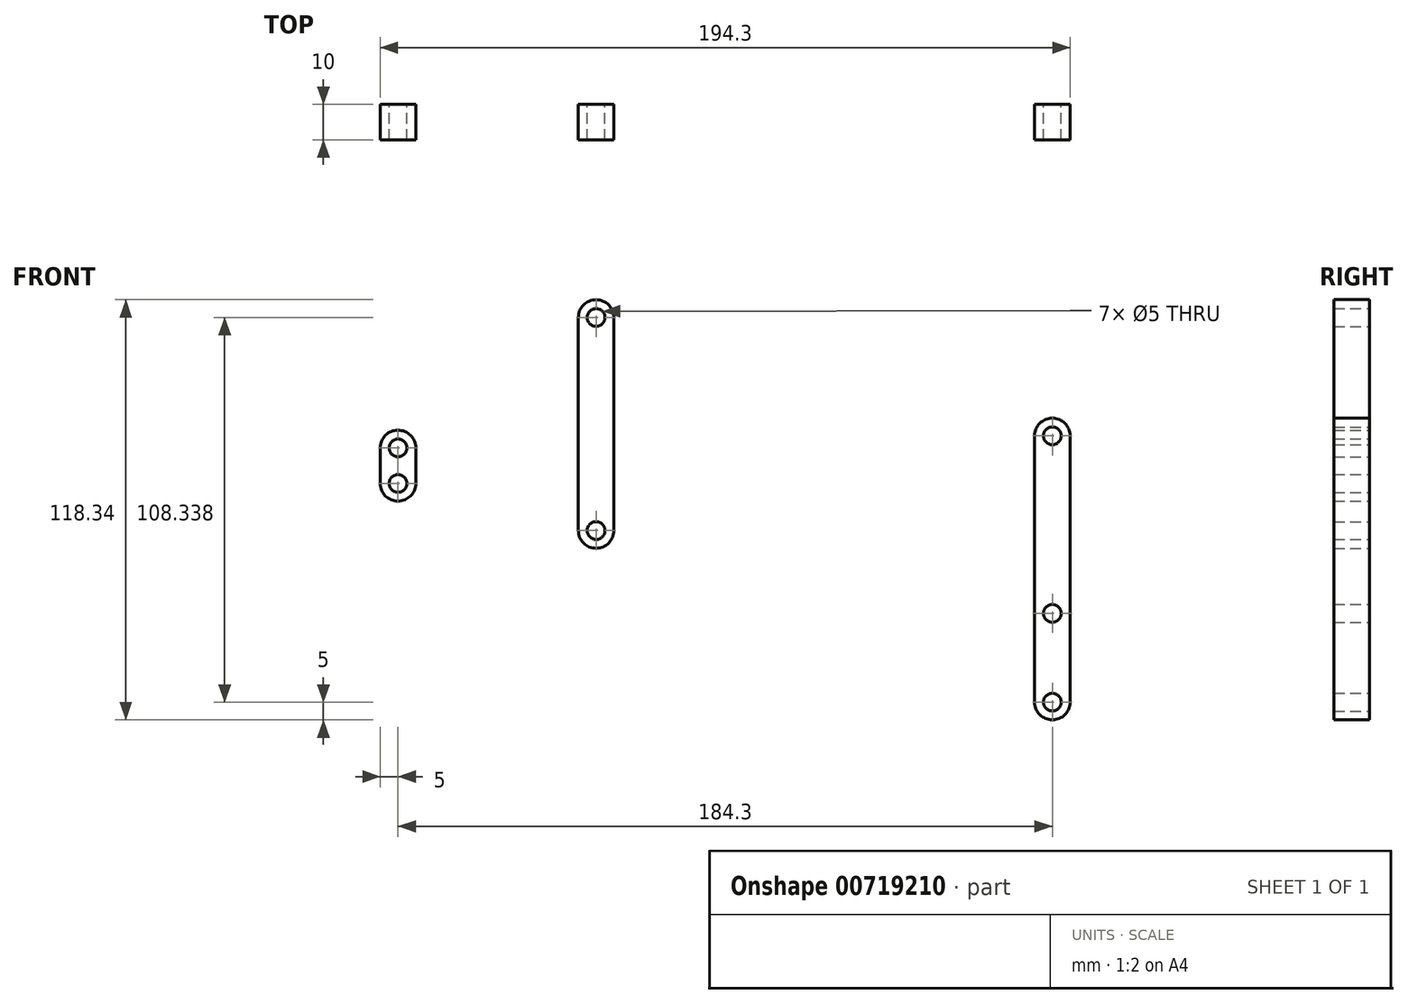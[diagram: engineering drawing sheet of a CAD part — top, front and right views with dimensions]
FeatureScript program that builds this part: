
annotation { "Feature Type Name" : "Feature", "Feature Type Description" : "" }
export const myFeature = defineFeature(function(context is Context, id is Id, definition is map)
    precondition{}
    {
        {
            var Q0;
            Q0=qCreatedBy(makeId("Front.planeOp"),FACE);
            var sketch = newSketch(context, id + "F0", { "sketchPlane" : qUnion([Q0])});
            skLineSegment(sketch, "E0.left", {"start": v(-5, 37.5) * mm, "end": v(-5, -37.5) * mm});
            skLineSegment(sketch, "E0.right", {"start": v(5, 37.5) * mm, "end": v(5, -37.5) * mm});
            skPoint(sketch, "E0.middle", {"position": v(0, 0) * mm});
            skArc(sketch, "E1", {"start": v(5, 37.5) * mm, "mid": v(0, 42.5) * mm, "end": v(-5, 37.5) * mm});
            skArc(sketch, "E2", {"start": v(-5, -37.5) * mm, "mid": v(0, -42.5) * mm, "end": v(5, -37.5) * mm});
            skCircle(sketch, "E3", {"center": v(0, 37.5) * mm, "radius": 2.5 * mm});
            skCircle(sketch, "E4", {"center": v(0, -37.5) * mm, "radius": 2.5 * mm});
            skCircle(sketch, "E5", {"center": v(0, -12.5) * mm, "radius": 2.5 * mm});
            skSolve(sketch);
        }
        {
            var Q0;
            Q0=makeQuery(id+"F0.imprint","IMPRINT",FACE,{"disambiguationData":[TD([[makeQuery(id+"F0.imprint","IMPRINT",EDGE,{"derivedFrom":sQuery(id+"F0.wireOp",EDGE,"E0.left")}),1.0]])]});
            extrude(context, id + "F1", {"entities" : qUnion([Q0]), "depth" : 10 * mm, "offsetDistance" : 25 * mm});
        }
        {
            var Q0;
            Q0=qCreatedBy(makeId("Front.planeOp"),FACE);
            var sketch = newSketch(context, id + "F2", { "sketchPlane" : qUnion([Q0])});
            skLineSegment(sketch, "E6.left", {"start": v(-133.5, 70.84) * mm, "end": v(-133.5, 10.84) * mm});
            skLineSegment(sketch, "E6.right", {"start": v(-123.5, 70.84) * mm, "end": v(-123.5, 10.84) * mm});
            skPoint(sketch, "E6.middle", {"position": v(-128.5, 40.84) * mm});
            skArc(sketch, "E7", {"start": v(-123.5, 70.84) * mm, "mid": v(-128.5, 75.84) * mm, "end": v(-133.5, 70.84) * mm});
            skArc(sketch, "E8", {"start": v(-133.5, 10.84) * mm, "mid": v(-128.5, 5.84) * mm, "end": v(-123.5, 10.84) * mm});
            skCircle(sketch, "E9", {"center": v(-128.5, 70.84) * mm, "radius": 2.5 * mm});
            skCircle(sketch, "E10", {"center": v(-128.5, 10.84) * mm, "radius": 2.5 * mm});
            skSolve(sketch);
        }
        {
            var Q0;
            Q0=makeQuery(id+"F2.imprint","IMPRINT",FACE,{"disambiguationData":[TD([[makeQuery(id+"F2.imprint","IMPRINT",EDGE,{"derivedFrom":sQuery(id+"F2.wireOp",EDGE,"E6.left")}),1.0]])]});
            extrude(context, id + "F3", {"entities" : qUnion([Q0]), "depth" : 10 * mm, "offsetDistance" : 25 * mm});
        }
        {
            var Q0;
            Q0=qCreatedBy(makeId("Front.planeOp"),FACE);
            var sketch = newSketch(context, id + "F4", { "sketchPlane" : qUnion([Q0])});
            skLineSegment(sketch, "E11.left", {"start": v(-189.3, 34.1) * mm, "end": v(-189.3, 24.1) * mm});
            skLineSegment(sketch, "E11.right", {"start": v(-179.3, 34.1) * mm, "end": v(-179.3, 24.1) * mm});
            skPoint(sketch, "E11.middle", {"position": v(-184.3, 29.1) * mm});
            skArc(sketch, "E12", {"start": v(-179.3, 34.1) * mm, "mid": v(-184.3, 39.1) * mm, "end": v(-189.3, 34.1) * mm});
            skArc(sketch, "E13", {"start": v(-189.3, 24.1) * mm, "mid": v(-184.3, 19.1) * mm, "end": v(-179.3, 24.1) * mm});
            skCircle(sketch, "E14", {"center": v(-184.3, 34.1) * mm, "radius": 2.5 * mm});
            skCircle(sketch, "E15", {"center": v(-184.3, 24.1) * mm, "radius": 2.5 * mm});
            skSolve(sketch);
        }
        {
            var Q0;
            Q0=makeQuery(id+"F4.imprint","IMPRINT",FACE,{"disambiguationData":[TD([[makeQuery(id+"F4.imprint","IMPRINT",EDGE,{"derivedFrom":sQuery(id+"F4.wireOp",EDGE,"E11.left")}),1.0]])]});
            extrude(context, id + "F5", {"entities" : qUnion([Q0]), "depth" : 10 * mm, "offsetDistance" : 25 * mm});
        }
    });
